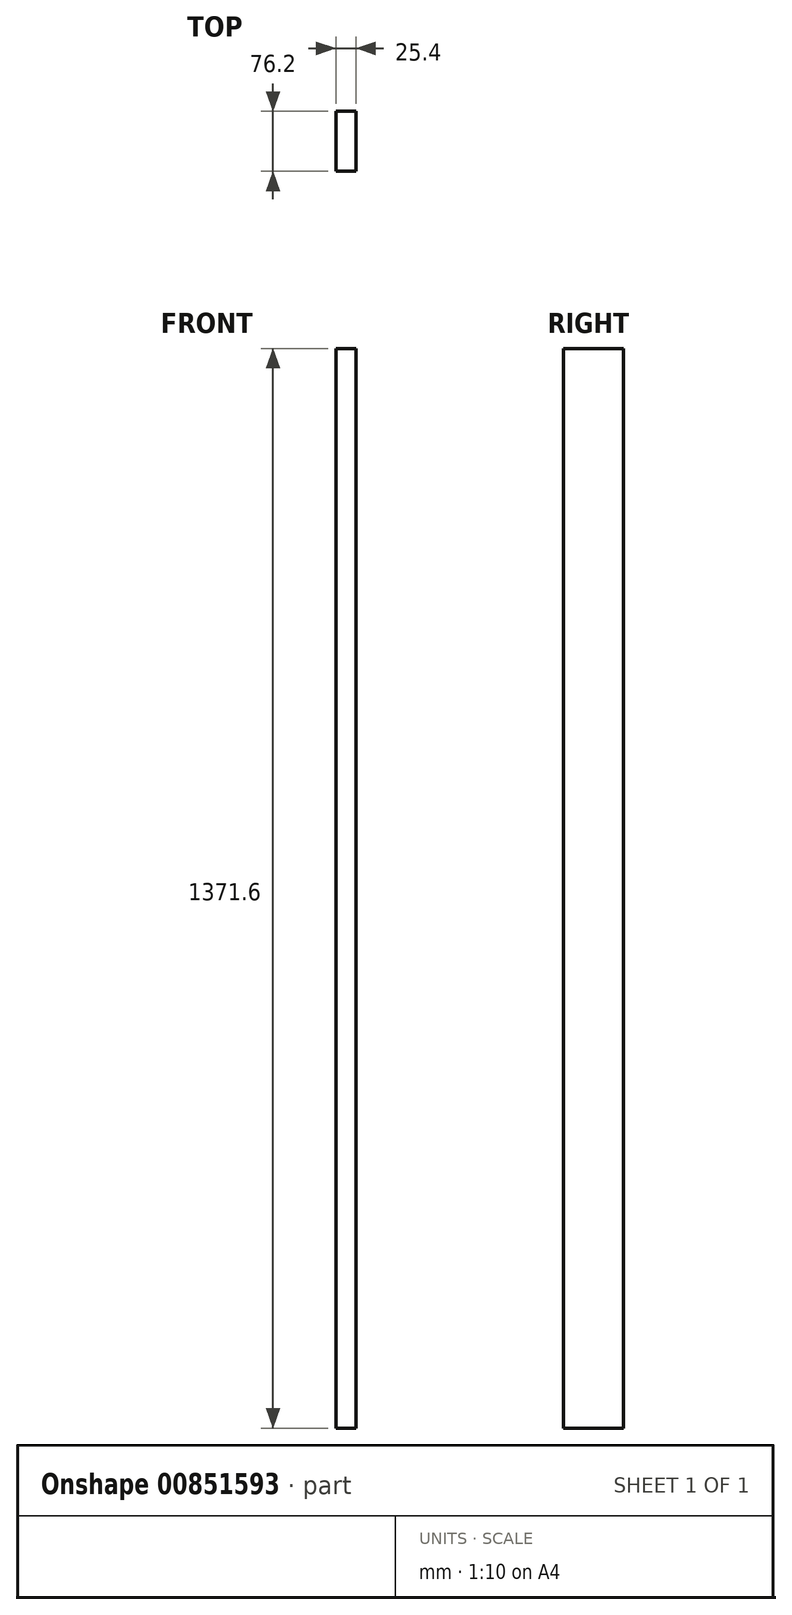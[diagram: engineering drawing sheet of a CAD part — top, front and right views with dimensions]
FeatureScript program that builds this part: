
annotation { "Feature Type Name" : "Feature", "Feature Type Description" : "" }
export const myFeature = defineFeature(function(context is Context, id is Id, definition is map)
    precondition{}
    {
        {
            var Q0;
            Q0=qCreatedBy(makeId("Front.planeOp"),FACE);
            var sketch = newSketch(context, id + "F0", { "sketchPlane" : qUnion([Q0])});
            skLineSegment(sketch, "E0.bottom", {"start": v(-36.55, 701.18) * mm, "end": v(-61.95, 701.18) * mm});
            skLineSegment(sketch, "E0.top", {"start": v(-36.55, -670.42) * mm, "end": v(-61.95, -670.42) * mm});
            skLineSegment(sketch, "E0.left", {"start": v(-36.55, 701.18) * mm, "end": v(-36.55, -670.42) * mm});
            skLineSegment(sketch, "E0.right", {"start": v(-61.95, 701.18) * mm, "end": v(-61.95, -670.42) * mm});
            skSolve(sketch);
        }
        {
            var Q0;
            Q0 = qSketchRegion(id + "F0", true);
            extrude(context, id + "F1", {"entities" : qUnion([Q0]), "depth" : 76.2 * mm, "offsetDistance" : 25.4 * mm});
        }
    });
